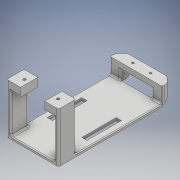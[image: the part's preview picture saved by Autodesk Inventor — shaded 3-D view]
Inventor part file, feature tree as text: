
AUTODESK INVENTOR PART (.ipt)
format: ipt  version: 2018 (Build 220112000, 112)  size: 360,960 bytes
history: native  units: mm
features: extrude x7, sketch x7, fillet x6, other x1, chamfer x1
ambient origin geometry x8: Origin, YZ Plane, XZ Plane, XY Plane, X Axis, Y Axis, Z Axis, Center Point
bodies: Body1 (feature_tree), Body2 (feature_tree), Body3 (feature_tree)
feature tree (22):
  other  "Sólido1"
  extrude  "Extrusión1"  Depth=100.0mm
  extrude  "Extrusión2"  Depth=10.0mm
  extrude  "Extrusión3"  Depth=10.0mm
  extrude  "Extrusión4"  Depth=3.0mm
  extrude  "Extrusión5"  Depth=6.0mm
  extrude  "Extrusión6"  Depth=6.0mm
  fillet  "Empalme1"  Radius=3.0mm
  chamfer  "Chaflán1"  Distance=20.0mm
  fillet  "Empalme5"  Radius=10.0mm
  extrude  "Extrusión8"  Depth=1.0mm
  fillet  "Empalme6"  Radius=13.0mm
  fillet  "Empalme7"  Radius=3.0mm
  fillet  "Empalme8"  Radius=10.25mm
  fillet  "Empalme9"  Radius=20.5mm
  sketch  "Boceto1"  dims[d0=40.0mm d1=100.0mm]
  sketch  "Boceto2"  dims[d2=10.0mm d3=10.0mm]
  sketch  "Boceto3"  dims[d4=10.0mm d5=10.0mm]
  sketch  "Boceto4"  dims[d6=20.0mm d7=3.0mm]
  sketch  "Boceto5"  dims[d8=40.0mm d9=6.0mm]
  sketch  "Boceto6"  dims[d10=3.0mm d11=6.0mm d12=3.0mm d13=0.0mm]
  sketch  "Boceto8"  dims[d14=45.0mm d15=20.0mm d16=10.0mm d17=18.0mm d18=13.0mm d19=3.0mm d20=0.0mm d21=10.25mm d22=20.5mm d24=2.5mm d25=2.5mm d26=3.0mm d27=0.0mm d28=7.0mm d29=7.0mm d30=17.5mm d31=0.0mm d32=14.0mm d33=28.0mm d34=10.0mm d35=11.0mm d36=45.0mm d37=11.0mm d38=18.5mm d39=0.0mm d40=10.0mm d41=3.0mm d42=18.5mm d43=0.0mm d44=2.0mm d46=7.0mm d47=2.0mm d48=45.0deg d51=1.0mm d54=8.0mm d57=5.0mm d58=7.75mm d59=18.5mm d60=0.0mm d61=2.0mm d62=7.0mm d63=2.0mm d64=1.0mm]
